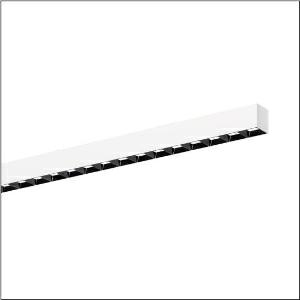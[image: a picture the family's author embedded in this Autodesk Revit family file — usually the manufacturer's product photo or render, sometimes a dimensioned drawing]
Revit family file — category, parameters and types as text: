
# Revit family: silica_r__21_51mx22tbt5w_cdcc
name_source: partatom
category: Lighting Fixtures
units: mm (PartAtom-declared; Revit-internal decimal feet)

## family parameters
Cut with Voids When Loaded = No
Host = Face
Light Source = No
Part Type = Normal
Room Calculation Point = No
Round Connector Dimension = Use Diameter
Shared = No

## types (1)
- --- (1 x LED, 4650 lm, 40.2 W, 6500K)
    Apparent Load = 40 VA
    CIE Flux Codes = 84 100 100 100 100
    Color Rendering = 80
    Color Temperature = 6500K
    Default Elevation = 1800 mm
    Description = Silica® 21, office luminaire, primary light control with darklight reflector, of PMMA, black, CAT 2 (L<= 3000cd/m²), light emission: direct distribution, primary light characteristic: symmetric, installation type: surface-mounted, LED, rated luminous flux: 4.650lm, luminous efficacy: 110lm/W, light colour: 8tw, colour temperature: 2700..6500K, control gear: ECG DALI, with terminal, 3+2-pole, max. 2.5mm², mains connection: 220..240V, AC, 50/60Hz, rated input power: 42.2W, luminaire housing, of aluminium, traffic white (RAL 9016), length: 1.504mm, width: 53mm, height: 53mm, protection rating (complete): IP20, insulation class (complete): insulation class I (protective earthing), certification: CE, permissible operating ambient temperature: 0..+35°C, standard: EN 50419, packaging unit: 1 piece
    Height = 0 mm  [stored 0 ft]
    Lamp = 1 x LED
    Lamp Light Flux = 4650 lm
    Lamp Power = 40.2 W
    Lamp count = 1
    Length = 1504 mm
    Luminous efficacy = 116 lm/W
    Manufacturer = Siteco
    ModVariant = No
    Model = 51MX22TBT5W
    Mounting Place = Ceiling
    Mounting Type = Recessed
    Number of Poles = 1
    OnlyDefault = Yes
    Power Factor = 1
    Product Name = Silica® 21
    Product group = office luminaire | ceiling recessed
    ProductGroupID = 400
    Protection Class = Protection class I
    Protection Degree = IP 20
    RLX_Detail_Level = 1
    RLX_Emergency_Light_Flux = 0 lm
    RLX_Emergency_Type = 0
    RLX_Emergency_Type_DB = No
    RlxData = <blob elided: 41361 chars, md5=16797141>
    Socket = socket
    Standby Power = 0 W
    System Light Flux = 4650 lm
    System Power = 40 W
    Type Comments = individual setting
    Type Image = l_1335873.jpg
    URL = http://relux.com
    VarID = @adj_109957
    Voltage = 0 V
    Weight = 0.00 kg
    Width = 53 mm

note: [stored X ft] marks values corroborated as IEEE doubles in the binary element streams (Revit-internal decimal feet)

## geometry (parser evidence)
native form markers: Blend x4, Sweep x10
no freeform markers — native parametric forms only
